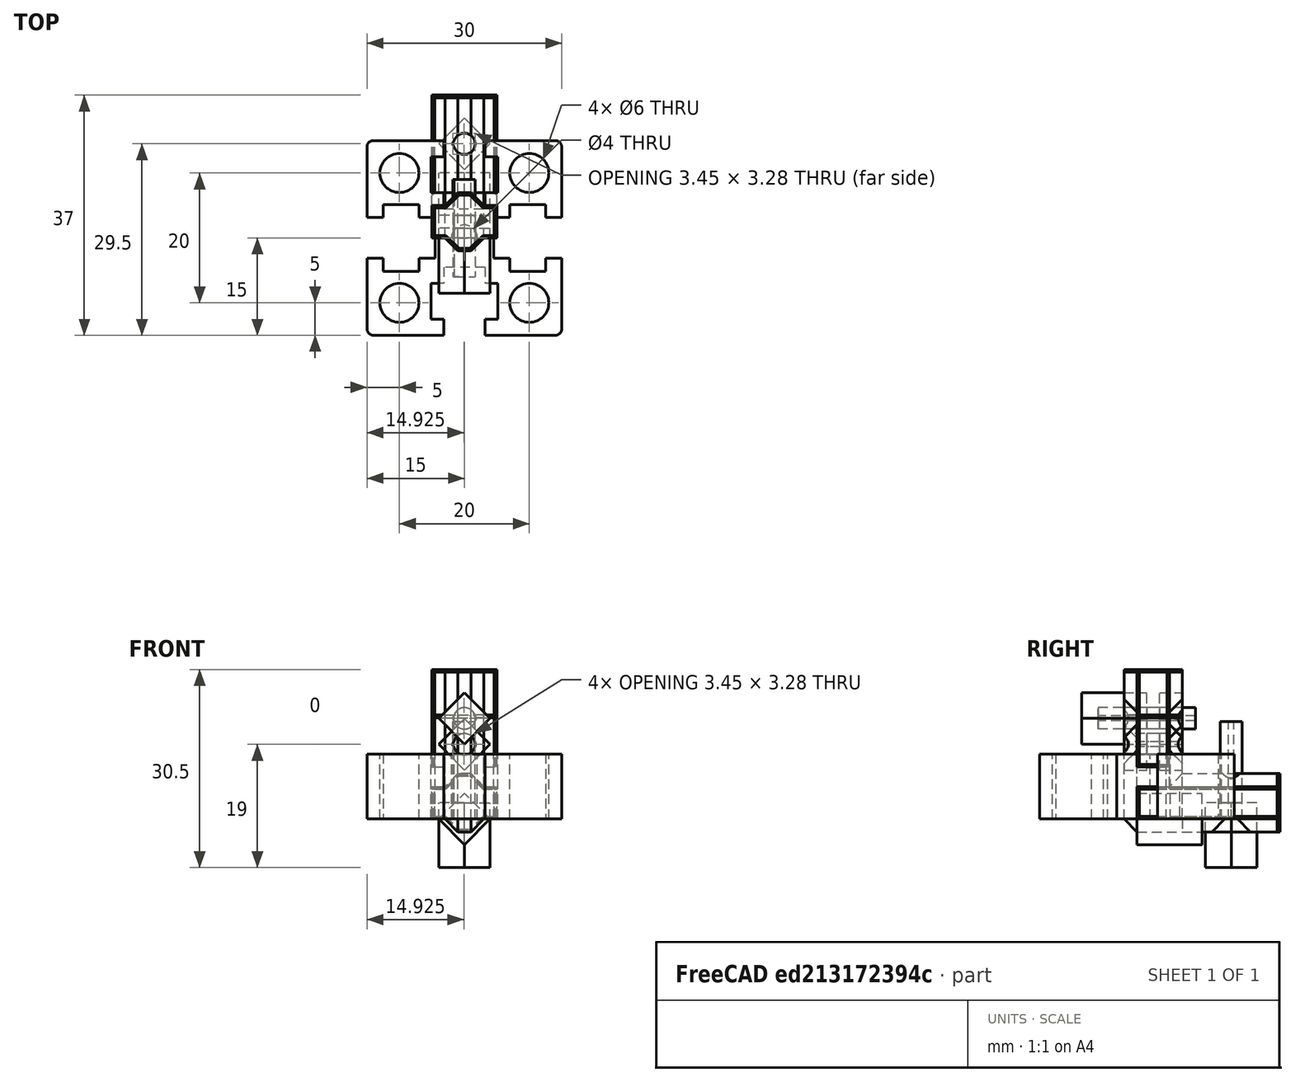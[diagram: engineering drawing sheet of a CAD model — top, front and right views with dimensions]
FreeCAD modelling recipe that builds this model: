
FCSTD DOCUMENT  (FreeCAD 0.18R16146 (Git))
Label: 3030-alpha-extrusion-joiner
License: All rights reserved
LicenseURL: http://en.wikipedia.org/wiki/All_rights_reserved
objects: Part::Feature×30, Part::Cut×19, Part::Box×11, Part::Cylinder×9, Part::Chamfer×8, Part::MultiFuse×4, Part::Fillet×1, App::DocumentObjectGroup×1
note: 82 computed .brp shape members not serialized (recipe doc carries the construction recipe); baked Part::Feature solids carry a one-line shape summary decoded from their .brp

FEATURE [Part::Box] Box002  label="Cube002"
  AttacherType = Attacher::AttachEngine3D
  Height = 10
  Length = 30
  Placement = pos=(-15,-15,0) rot=(0,0,1;0rad)
  Width = 30
FEATURE [Part::Feature] Fusion001
  Placement = pos=(0,4.5,0) rot=(0,0,1;0rad)
  shape: bbox 10.3 x 10.5 x 10 mm, 22 faces (baked)
FEATURE [Part::Feature] Fusion002
  Placement = pos=(4.5,-1.1e-15,0) rot=(0,0,-1;1.5708rad)
  shape: bbox 10.5 x 10.3 x 10 mm, 22 faces (baked)
FEATURE [Part::Feature] Fusion003
  Placement = pos=(-1e-15,-4.5,0) rot=(0,0,1;3.14159rad)
  shape: bbox 10.3 x 10.5 x 10 mm, 22 faces (baked)
FEATURE [Part::Feature] Fusion004
  Placement = pos=(-4.5,0,0) rot=(0,0,1;1.5708rad)
  shape: bbox 10.5 x 10.3 x 10 mm, 22 faces (baked)
FEATURE [Part::Cylinder] Cylinder
  Angle = 360
  AttacherType = Attacher::AttachEngine3D
  Height = 10
  Placement = pos=(10,10,0) rot=(0,0,1;0rad)
  Radius = 3
FEATURE [Part::Cylinder] Cylinder001
  Angle = 360
  AttacherType = Attacher::AttachEngine3D
  Height = 10
  Radius = 2
FEATURE [Part::Cylinder] Cylinder002
  Angle = 360
  AttacherType = Attacher::AttachEngine3D
  Height = 10
  Placement = pos=(-10,10,0) rot=(0,0,1;0rad)
  Radius = 3
FEATURE [Part::Cylinder] Cylinder003
  Angle = 360
  AttacherType = Attacher::AttachEngine3D
  Height = 10
  Placement = pos=(10,-10,0) rot=(0,0,1;0rad)
  Radius = 3
FEATURE [Part::Cylinder] Cylinder004
  Angle = 360
  AttacherType = Attacher::AttachEngine3D
  Height = 10
  Placement = pos=(-10,-10,0) rot=(0,0,1;0rad)
  Radius = 3
FEATURE [Part::Feature] Box006001001  label="square-nut-template"
  shape: bbox 7.92 x 10 x 7.92 mm, 6 faces (baked)
FEATURE [Part::Box] Box006001002  label="Cube006"
  AttacherType = Attacher::AttachEngine3D
  Height = 5
  Length = 10
  Width = 22
FEATURE [Part::Box] Box006001003  label="Cube007"
  AttacherType = Attacher::AttachEngine3D
  Height = 15
  Length = 10
  Placement = pos=(0,0,8) rot=(0,0,1;0rad)
  Width = 5
FEATURE [Part::Box] Box006001004  label="Cube008"
  AttacherType = Attacher::AttachEngine3D
  Height = 9
  Length = 6
  Placement = pos=(2,0,-2) rot=(0,0,1;0rad)
  Width = 22
FEATURE [Part::Box] Box006001005  label="Cube009"
  AttacherType = Attacher::AttachEngine3D
  Height = 25
  Length = 6
  Placement = pos=(2,-2,-2) rot=(0,0,1;0rad)
  Width = 9
FEATURE [Part::Chamfer] Chamfer002
  Base = -> Box006001004
  Edges = 4 edges r=2: [Edge2,Edge4,Edge6,Edge8]
FEATURE [Part::Chamfer] Chamfer003
  Base = -> Box006001005
  Edges = 7 edges r=2: [Edge1,Edge3,Edge4,Edge5,Edge7,Edge8,Edge9]
FEATURE [Part::MultiFuse] Fusion006002004
  Placement = pos=(-5,0,0) rot=(0,0,1;0rad)
  Shapes = -> [Box006001002,Chamfer003,Chamfer002,Box006001003]
FEATURE [Part::Feature] Box006001006  label="square-nut-template001"
  Placement = pos=(0,-8.5,15.5) rot=(0,0,1;0rad)
  shape: bbox 7.92 x 10 x 7.92 mm, 6 faces (baked)
FEATURE [Part::Feature] Box006001007  label="square-nut-template002"
  Placement = pos=(0,14.5,-7.5) rot=(1,0,0;1.5708rad)
  shape: bbox 7.92 x 7.92 x 10 mm, 6 faces (baked)
FEATURE [Part::Cylinder] Cylinder005
  Angle = 360
  AttacherType = Attacher::AttachEngine3D
  Height = 15
  Placement = pos=(0,14.5,0) rot=(0,0,1;0rad)
  Radius = 1.65
FEATURE [Part::Cylinder] Cylinder006
  Angle = 360
  AttacherType = Attacher::AttachEngine3D
  Height = 15
  Placement = pos=(0,9,15.5) rot=(1,0,0;1.5708rad)
  Radius = 1.65
FEATURE [Part::Cylinder] Cylinder007
  Angle = 360
  AttacherType = Attacher::AttachEngine3D
  Height = 15
  Placement = pos=(-1.3,9,15.5) rot=(1,0,0;1.5708rad)
  Radius = 0.5
FEATURE [Part::Cylinder] Cylinder008
  Angle = 360
  AttacherType = Attacher::AttachEngine3D
  Height = 15
  Placement = pos=(-1.3,14.5,0) rot=(0,0,1;0rad)
  Radius = 0.5
FEATURE [Part::MultiFuse] Fusion006002006
  Shapes = -> [Cylinder004,Fusion001,Fusion003,Fusion004,Fusion002,Cylinder,Cylinder002,Cylinder001,Cylinder003]
FEATURE [Part::Fillet] Fillet
  Base = -> Box002
  Edges = 4 edges r=1: [Edge1,Edge3,Edge5,Edge7]
FEATURE [Part::Cut] Cut  label="extrusion-template"
  Base = -> Fillet
  Tool = -> Fusion006002006
FEATURE [Part::Feature] Cut001001  label="Cut002"
  shape: bbox 10 x 24 x 25 mm, 57 faces (baked)
FEATURE [Part::Chamfer] Chamfer  label="L-shape"
  Base = -> Cut001001
  Edges = 36 edges r=0.2: [Edge1,Edge2,Edge3,Edge4,Edge8,Edge11,Edge26,Edge31,Edge54,Edge55,Edge62,Edge70,Edge73,Edge74,Edge106,Edge107,Edge108,Edge112,Edge120,Edge121,Edge122,Edge124,Edge125,Edge128,Edge129,Edge130,Edge131,Edge136,Edge137,Edge145,Edge148,Edge151,Edge152,Edge153,Edge154,Edge155]
FEATURE [Part::Feature] Fusion006002008001  label="L-shape-rev001"
  shape: bbox 10 x 24 x 25 mm, 109 faces (baked)
FEATURE [Part::Box] Box006001009  label="Cube011"
  AttacherType = Attacher::AttachEngine3D
  Height = 11
  Length = 12
  Placement = pos=(-6,7,-3) rot=(0,0,1;0rad)
  Width = 16
FEATURE [Part::Cut] Cut001003
  Base = -> Fusion006002008001
  Tool = -> Box006001009
FEATURE [Part::Feature] Fusion006002004001  label="Fusion006002008"
  Placement = pos=(-5,0,0) rot=(0,0,1;0rad)
  shape: bbox 10 x 24 x 25 mm, 46 faces (baked)
FEATURE [Part::MultiFuse] Fusion
  Shapes = -> [Cylinder006,Cylinder007]
FEATURE [Part::MultiFuse] Fusion006002008002
  Shapes = -> [Cylinder005,Cylinder008]
FEATURE [App::DocumentObjectGroup] Group  label="origin"
  Group = -> [Box006001006,Fusion006002004001,Fusion006002008002,Fusion,Box006001007]
FEATURE [Part::Feature] Box006001006001  label="square-nut-template003"
  Placement = pos=(0,3.5,15.5) rot=(0,0,1;0rad)
  shape: bbox 7.92 x 10 x 7.92 mm, 6 faces (baked)
FEATURE [Part::Feature] Fusion006002004001001  label="Fusion006002008003"
  Placement = pos=(-5,0,0) rot=(0,0,1;0rad)
  shape: bbox 10 x 24 x 25 mm, 46 faces (baked)
FEATURE [Part::Feature] Fusion006002008002002  label="Fusion006002008005"
  shape: bbox 3.45 x 15 x 3.3 mm, 9 faces (baked)
FEATURE [Part::Cut] Cut001004
  Base = -> Fusion006002004001001
  Tool = -> Box006001006001
FEATURE [Part::Cut] Cut001005  label="rev-l-base"
  Base = -> Cut001004
  Tool = -> Fusion006002008002002
FEATURE [Part::Feature] Cut001005001  label="rev-l-base001"
  shape: bbox 10 x 24 x 25 mm, 46 faces (baked)
FEATURE [Part::Chamfer] Chamfer004  label="L-shape-rev"
  Base = -> Cut001005001
  Edges = 36 edges r=0.4: [Edge1,Edge2,Edge5,Edge6,Edge7,Edge8,Edge12,Edge13,Edge14,Edge15,Edge19,Edge22,Edge30,Edge35,Edge48,Edge50,Edge51,Edge55,Edge59,Edge65,Edge75,Edge76,Edge85,Edge87,Edge90,Edge91,Edge105,Edge107,Edge108,Edge109,Edge110,Edge113,Edge114,Edge115,Edge116,Edge117]
FEATURE [Part::Feature] Fusion006002004001002  label="Fusion006002008008"
  Placement = pos=(-5,0,0) rot=(0,0,1;0rad)
  shape: bbox 10 x 24 x 25 mm, 46 faces (baked)
FEATURE [Part::Feature] Box006001006002  label="square-nut-template005"
  Placement = pos=(0,3.5,15.5) rot=(0,0,1;0rad)
  shape: bbox 7.92 x 10 x 7.92 mm, 6 faces (baked)
FEATURE [Part::Feature] Fusion006002008002004  label="Fusion006002008009"
  shape: bbox 3.45 x 15 x 3.3 mm, 9 faces (baked)
FEATURE [Part::Box] Box  label="Cube"
  AttacherType = Attacher::AttachEngine3D
  Height = 13
  Length = 12
  Placement = pos=(-6,7,-4) rot=(0,0,1;0rad)
  Width = 25
FEATURE [Part::Cut] Cut001005002
  Base = -> Fusion006002004001002
  Tool = -> Box
FEATURE [Part::Cut] Cut001005003
  Base = -> Cut001005002
  Tool = -> Box006001006002
FEATURE [Part::Cut] Cut001005004  label="head-join-base"
  Base = -> Cut001005003
  Tool = -> Fusion006002008002004
FEATURE [Part::Feature] Cut001005004001  label="head-join-base001"
  shape: bbox 10 x 9 x 25 mm, 44 faces (baked)
FEATURE [Part::Chamfer] Chamfer005
  Base = -> Cut001005004001
  Edges = 26 edges r=0.4: [Edge10,Edge11,Edge12,Edge13,Edge32,Edge39,Edge47,Edge48,Edge49,Edge57,Edge58,Edge59,Edge66,Edge69,Edge70,Edge71,Edge85,Edge86,Edge93,Edge95,Edge105,Edge108,Edge109,Edge111,Edge112,Edge113]
FEATURE [Part::Feature] Box006001006003  label="square-nut-template006"
  Placement = pos=(0,-8.5,11.5) rot=(0,0,1;0rad)
  shape: bbox 7.92 x 10 x 7.92 mm, 6 faces (baked)
FEATURE [Part::Feature] Box006001007001  label="square-nut-template007"
  Placement = pos=(0,14.5,-7.5) rot=(1,0,0;1.5708rad)
  shape: bbox 7.92 x 7.92 x 10 mm, 6 faces (baked)
FEATURE [Part::Feature] Fusion006002004001003  label="Fusion006002008010"
  Placement = pos=(-5,0,0) rot=(0,0,1;0rad)
  shape: bbox 10 x 24 x 25 mm, 46 faces (baked)
FEATURE [Part::Feature] Fusion006002008002005  label="Fusion006002008011"
  shape: bbox 3.45 x 3.3 x 15 mm, 9 faces (baked)
FEATURE [Part::Feature] Fusion006002008002006  label="Fusion006002008012"
  Placement = pos=(0,0,-4) rot=(0,0,1;0rad)
  shape: bbox 3.45 x 15 x 3.3 mm, 9 faces (baked)
FEATURE [Part::Cut] Cut001005004002
  Base = -> Fusion006002004001003
  Tool = -> Fusion006002008002006
FEATURE [Part::Cut] Cut001005004003
  Base = -> Cut001005004002
  Tool = -> Box006001006003
FEATURE [Part::Cut] Cut001005004004
  Base = -> Cut001005004003
  Tool = -> Fusion006002008002005
FEATURE [Part::Cut] Cut001005004005
  Base = -> Cut001005004004
  Tool = -> Box006001007001
FEATURE [Part::Box] Box006001007002  label="Cube012"
  AttacherType = Attacher::AttachEngine3D
  Height = 10
  Length = 15
  Placement = pos=(-7,-3,16) rot=(0,0,1;0rad)
  Width = 15
FEATURE [Part::Cut] Cut001005004006
  Base = -> Cut001005004005
  Tool = -> Box006001007002
FEATURE [Part::Feature] Cut001005004006001  label="Cut001005004007"
  shape: bbox 10 x 24 x 18 mm, 57 faces (baked)
FEATURE [Part::Chamfer] Chamfer006  label="short-L"
  Base = -> Cut001005004006001
  Edges = 36 edges r=0.4: [Edge1,Edge2,Edge3,Edge4,Edge8,Edge11,Edge26,Edge31,Edge54,Edge55,Edge62,Edge70,Edge73,Edge74,Edge106,Edge107,Edge108,Edge109,Edge110,Edge111,Edge112,Edge113,Edge114,Edge115,Edge116,Edge120,Edge128,Edge130,Edge131,Edge134,Edge135,Edge136,Edge137,Edge142,Edge154,Edge155]
FEATURE [Part::Feature] Box006001006004  label="square-nut-template008"
  Placement = pos=(0,0,-4) rot=(0,0,1;0rad)
  shape: bbox 7.92 x 10 x 7.92 mm, 6 faces (baked)
FEATURE [Part::Feature] Fusion006002004001004  label="Fusion006002008013"
  shape: bbox 10 x 24 x 25 mm, 35 faces (baked)
FEATURE [Part::Feature] Fusion006002008002008  label="Fusion006002008015"
  Placement = pos=(0,0,-4) rot=(0,0,1;0rad)
  shape: bbox 3.45 x 15 x 3.3 mm, 4 faces (baked)
FEATURE [Part::Cut] Cut001005004006002
  Base = -> Fusion006002004001004
  Tool = -> Fusion006002008002008
FEATURE [Part::Cut] Cut001005004006003
  Base = -> Cut001005004006002
  Tool = -> Box006001006004
FEATURE [Part::Box] Box006001007003  label="Cube013"
  AttacherType = Attacher::AttachEngine3D
  Height = 10
  Length = 13
  Placement = pos=(-6,-2,16) rot=(0,0,1;0rad)
  Width = 10
FEATURE [Part::Cut] Cut001005004006004
  Base = -> Cut001005004006003
  Tool = -> Box006001007003
FEATURE [Part::Box] Box006001007004  label="Cube014"
  AttacherType = Attacher::AttachEngine3D
  Height = 19
  Length = 13
  Placement = pos=(-7,7,-4) rot=(0,0,1;0rad)
  Width = 16
FEATURE [Part::Cut] Cut001005004006005
  Base = -> Cut001005004006004
  Tool = -> Box006001007004
FEATURE [Part::Chamfer] Chamfer007  label="short-head"
  Base = -> Cut001005004006005
  Edges = 26 edges r=0.4: [Edge2,Edge7,Edge12,Edge16,Edge17,Edge26,Edge27,Edge28,Edge51,Edge65,Edge79,Edge80,Edge85,Edge86,Edge87,Edge88,Edge89,Edge90,Edge91,Edge92,Edge93,Edge95,Edge97,Edge101,Edge102,Edge116]
FEATURE [Part::Feature] Box006001006005  label="square-nut-template009"
  Placement = pos=(0,12,-4) rot=(0,0,1;0rad)
  shape: bbox 7.92 x 10 x 7.92 mm, 6 faces (baked)
FEATURE [Part::Feature] Fusion006002004001005  label="Fusion006002008016"
  shape: bbox 10 x 24 x 25 mm, 35 faces (baked)
FEATURE [Part::Feature] Fusion006002008002010  label="Fusion006002008018"
  Placement = pos=(0,0,-4) rot=(0,0,1;0rad)
  shape: bbox 3.45 x 15 x 3.3 mm, 4 faces (baked)
FEATURE [Part::Cut] Cut001005004006006
  Base = -> Fusion006002004001005
  Tool = -> Box006001006005
FEATURE [Part::Cut] Cut001005004006007
  Base = -> Cut001005004006006
  Tool = -> Fusion006002008002010
FEATURE [Part::Box] Box006001007005  label="Cube015"
  AttacherType = Attacher::AttachEngine3D
  Height = 15
  Length = 17
  Placement = pos=(-8,-3,16) rot=(0,0,1;0rad)
  Width = 14
FEATURE [Part::Cut] Cut001005004006008
  Base = -> Cut001005004006007
  Tool = -> Box006001007005
FEATURE [Part::Chamfer] Chamfer008  label="short-rev-L"
  Base = -> Cut001005004006008
  Edges = 36 edges r=0.4: [Edge1,Edge2,Edge5,Edge6,Edge7,Edge8,Edge9,Edge10,Edge11,Edge12,Edge13,Edge14,Edge15,Edge16,Edge17,Edge24,Edge25,Edge26,Edge44,Edge73,Edge75,Edge76,Edge77,Edge78,Edge79,Edge80,Edge81,Edge82,Edge83,Edge84,Edge86,Edge91,Edge98,Edge103,Edge106,Edge110]
